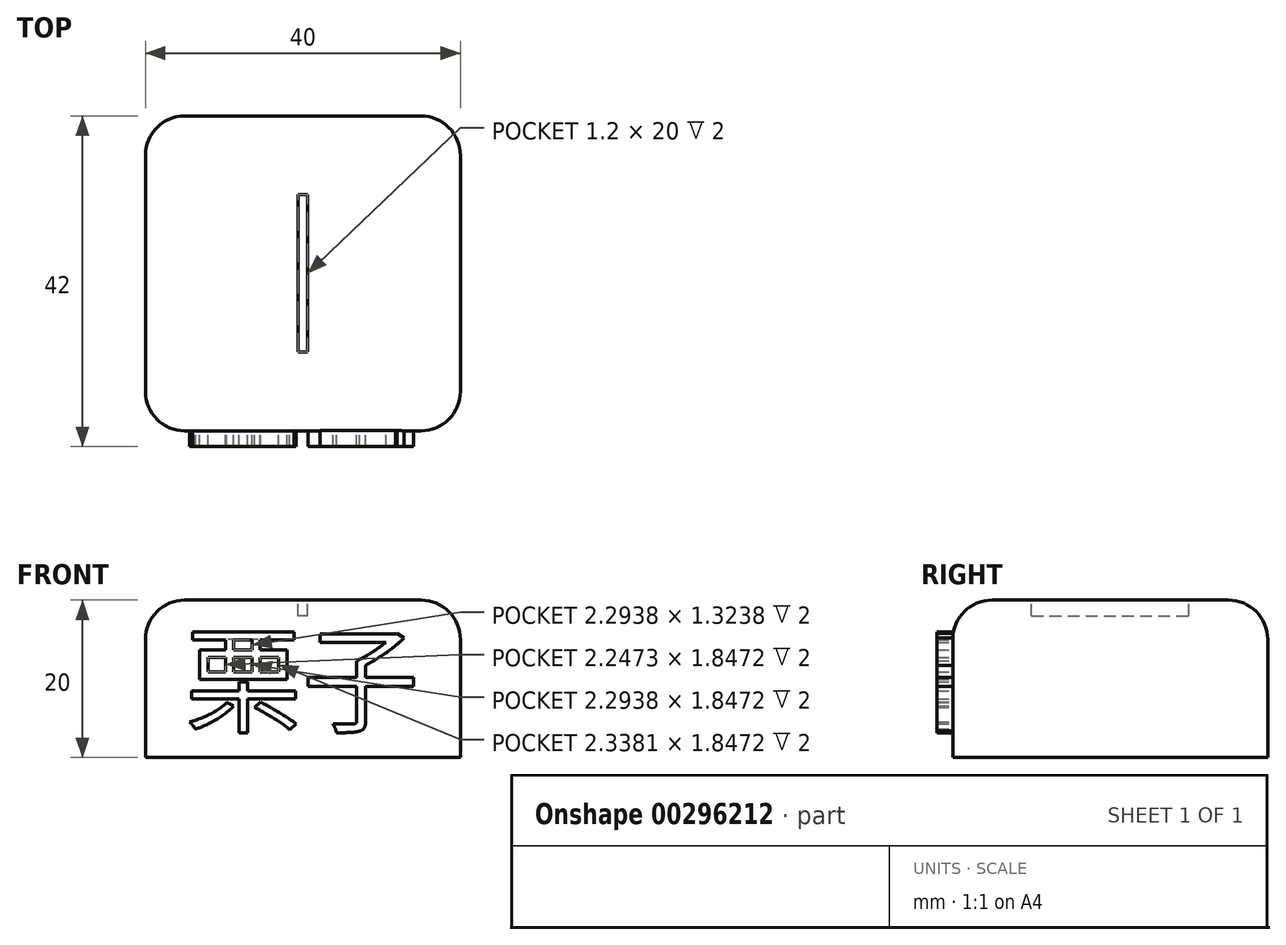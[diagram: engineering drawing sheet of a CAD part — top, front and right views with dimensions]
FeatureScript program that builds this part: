
annotation { "Feature Type Name" : "Feature", "Feature Type Description" : "" }
export const myFeature = defineFeature(function(context is Context, id is Id, definition is map)
    precondition{}
    {
        {
            var Q0;
            Q0=qCreatedBy(makeId("Top.planeOp"),FACE);
            var sketch = newSketch(context, id + "F0", { "sketchPlane" : qUnion([Q0])});
            skLineSegment(sketch, "E0.bottom", {"start": v(20, -20) * mm, "end": v(-20, -20) * mm});
            skLineSegment(sketch, "E0.top", {"start": v(20, 20) * mm, "end": v(-20, 20) * mm});
            skLineSegment(sketch, "E0.left", {"start": v(20, -20) * mm, "end": v(20, 20) * mm});
            skLineSegment(sketch, "E0.right", {"start": v(-20, -20) * mm, "end": v(-20, 20) * mm});
            skPoint(sketch, "E0.middle", {"position": v(0, 0) * mm});
            skLineSegment(sketch, "E1.bottom", {"start": v(0.6, -10) * mm, "end": v(-0.6, -10) * mm});
            skLineSegment(sketch, "E1.top", {"start": v(0.6, 10) * mm, "end": v(-0.6, 10) * mm});
            skLineSegment(sketch, "E1.left", {"start": v(0.6, -10) * mm, "end": v(0.6, 10) * mm});
            skLineSegment(sketch, "E1.right", {"start": v(-0.6, -10) * mm, "end": v(-0.6, 10) * mm});
            skSolve(sketch);
        }
        {
            var Q0;
            Q0=makeQuery(id+"F0.imprint","IMPRINT",FACE,{"disambiguationData":[TD([[makeQuery(id+"F0.imprint","IMPRINT",EDGE,{"derivedFrom":sQuery(id+"F0.wireOp",EDGE,"E0.bottom")}),-1.0]])]});
            var Q1;
            Q1=makeQuery(id+"F0.imprint","IMPRINT",FACE,{"disambiguationData":[TD([[makeQuery(id+"F0.imprint","IMPRINT",EDGE,{"derivedFrom":sQuery(id+"F0.wireOp",EDGE,"E1.bottom")}),-1.0]])]});
            extrude(context, id + "F1", {"entities" : qUnion([Q0, Q1]), "oppositeDirection" : true, "depth" : 20 * mm});
        }
        {
            var Q0;
            Q0=makeQuery(id+"F0.imprint","IMPRINT",FACE,{"disambiguationData":[TD([[makeQuery(id+"F0.imprint","IMPRINT",EDGE,{"derivedFrom":sQuery(id+"F0.wireOp",EDGE,"E1.bottom")}),-1.0]])]});
            extrude(context, id + "F2", {"entities" : qUnion([Q0]), "operationType" : NewBodyOperationType.REMOVE, "oppositeDirection" : true, "depth" : 2 * mm});
        }
        {
            var Q0;
            Q0=makeQuery(id+"F2.boolean.opBoolean","COPY",EDGE,{"derivedFrom":makeQuery(id+"F2.opExtrude","CAP_EDGE",EDGE,{"disambiguationData":[OSD([sQuery(id+"F0.wireOp",EDGE,"E1.left")])],"isStart":true})});
            var Q1;
            Q1=makeQuery(id+"F2.boolean.opBoolean","COPY",EDGE,{"derivedFrom":makeQuery(id+"F2.opExtrude","CAP_EDGE",EDGE,{"disambiguationData":[OSD([sQuery(id+"F0.wireOp",EDGE,"E1.right")])],"isStart":true})});
            var Q2;
            Q2=makeQuery(id+"F1.opExtrude","SWEPT_EDGE",EDGE,{"disambiguationData":[OSD([sQuery(id+"F0.wireOp",EDGE,"E0.bottom"),sQuery(id+"F0.wireOp",EDGE,"E0.left")])]});
            var Q3;
            Q3=makeQuery(id+"F1.opExtrude","SWEPT_EDGE",EDGE,{"disambiguationData":[OSD([sQuery(id+"F0.wireOp",EDGE,"E0.top"),sQuery(id+"F0.wireOp",EDGE,"E0.left")])]});
            var Q4;
            Q4=makeQuery(id+"F1.opExtrude","CAP_EDGE",EDGE,{"disambiguationData":[OSD([sQuery(id+"F0.wireOp",EDGE,"E0.left")])],"isStart":true});
            var Q5;
            Q5=makeQuery(id+"F1.opExtrude","SWEPT_EDGE",EDGE,{"disambiguationData":[OSD([sQuery(id+"F0.wireOp",EDGE,"E0.bottom"),sQuery(id+"F0.wireOp",EDGE,"E0.right")])]});
            var Q6;
            Q6=makeQuery(id+"F1.opExtrude","SWEPT_EDGE",EDGE,{"disambiguationData":[OSD([sQuery(id+"F0.wireOp",EDGE,"E0.top"),sQuery(id+"F0.wireOp",EDGE,"E0.right")])]});
            var Q7;
            Q7=makeQuery(id+"F1.opExtrude","CAP_EDGE",EDGE,{"disambiguationData":[OSD([sQuery(id+"F0.wireOp",EDGE,"E0.top")])],"isStart":true});
            var Q8;
            Q8=makeQuery(id+"F1.opExtrude","CAP_EDGE",EDGE,{"disambiguationData":[OSD([sQuery(id+"F0.wireOp",EDGE,"E0.right")])],"isStart":true});
            var Q9;
            Q9=makeQuery(id+"F1.opExtrude","CAP_EDGE",EDGE,{"disambiguationData":[OSD([sQuery(id+"F0.wireOp",EDGE,"E0.bottom")])],"isStart":true});
            fillet(context, id + "F3", {"entities" : qUnion([Q0, Q1, Q2, Q3, Q4, Q5, Q6, Q7, Q8, Q9]), "radius" : 5 * mm, "tangentPropagation" : true, "allowEdgeOverflow" : false});
        }
        {
            var Q0;
            Q0=makeQuery(id+"F1.opExtrude","SWEPT_FACE",FACE,{"disambiguationData":[OSD([sQuery(id+"F0.wireOp",EDGE,"E0.bottom")])]});
            var sketch = newSketch(context, id + "F4", { "sketchPlane" : qUnion([Q0])});
            skText(sketch, "E2", { "text": "栗子", "fontName": "NotoSansCJKtc-Regular.otf"});
            const initialGuessF4  = {"E2": [-0.015, -0.01572, 1, 0, 0.01072]};
            skSetInitialGuess(sketch, initialGuessF4);
            skSolve(sketch);
        }
        {
            var Q0;
            Q0=makeQuery(id+"F4.imprint","IMPRINT",FACE,{"disambiguationData":[TD([[makeQuery(id+"F4.imprint","IMPRINT",EDGE,{"derivedFrom":sQuery(id+"F4.wireOp",EDGE,"E2.sketch_text.stroke-0")}),1.0]])]});
            var Q1;
            {var subQ1=sQuery(id+"F4.wireOp",EDGE,"E2.sketch_text.stroke-51");Q1=makeQuery(id+"F4.imprint","IMPRINT",FACE,{"disambiguationData":[TD([[makeQuery(id+"F4.imprint","IMPRINT",EDGE,{"derivedFrom":subQ1}),1.0]])]});}
            var Q2;
            {var subQ0=sQuery(id+"F4.wireOp",EDGE,"E2.sketch_text.stroke-24");Q2=makeQuery(id+"F4.imprint","IMPRINT",FACE,{"disambiguationData":[TD([[makeQuery(id+"F4.imprint","IMPRINT",EDGE,{"derivedFrom":subQ0}),1.0]])]});}
            var Q3;
            Q3=makeQuery(id+"F4.imprint","IMPRINT",FACE,{"disambiguationData":[TD([[makeQuery(id+"F4.imprint","IMPRINT",EDGE,{"derivedFrom":sQuery(id+"F4.wireOp",EDGE,"E2.sketch_text.stroke-32")}),1.0]])]});
            var Q4;
            Q4=makeQuery(id+"F4.imprint","IMPRINT",FACE,{"disambiguationData":[TD([[makeQuery(id+"F4.imprint","IMPRINT",EDGE,{"derivedFrom":sQuery(id+"F4.wireOp",EDGE,"E2.sketch_text.stroke-28")}),1.0]])]});
            var Q5;
            Q5=makeQuery(id+"F4.imprint","IMPRINT",FACE,{"disambiguationData":[TD([[makeQuery(id+"F4.imprint","IMPRINT",EDGE,{"derivedFrom":sQuery(id+"F4.wireOp",EDGE,"E2.sketch_text.stroke-44")}),1.0]])]});
            extrude(context, id + "F5", {"entities" : qUnion([Q0, Q1, Q2, Q3, Q4, Q5]), "operationType" : NewBodyOperationType.ADD, "depth" : 2 * mm});
        }
        {
            var Q0;
            Q0=makeQuery(id+"F5.opExtrude","CAP_FACE",FACE,{"disambiguationData":[OSD([sQuery(id+"F0.wireOp",EDGE,"E0.bottom"),sQuery(id+"F4.wireOp",EDGE,"E2.sketch_text.stroke-50"),sQuery(id+"F4.wireOp",EDGE,"E2.sketch_text.stroke-51"),sQuery(id+"F4.wireOp",EDGE,"E2.sketch_text.stroke-52"),sQuery(id+"F4.wireOp",EDGE,"E2.sketch_text.stroke-53"),sQuery(id+"F4.wireOp",EDGE,"E2.sketch_text.stroke-54")])],"isStart":false});
            extrude(context, id + "F6", {"entities" : qUnion([Q0]), "operationType" : NewBodyOperationType.ADD, "oppositeDirection" : true, "depth" : 3 * mm});
        }
        {
            var Q0;
            Q0=makeQuery(id+"F4.imprint","IMPRINT",FACE,{"disambiguationData":[TD([[makeQuery(id+"F4.imprint","IMPRINT",EDGE,{"derivedFrom":sQuery(id+"F4.wireOp",EDGE,"E2.sketch_text.stroke-48")}),1.0]])]});
            extrude(context, id + "F7", {"entities" : qUnion([Q0]), "operationType" : NewBodyOperationType.ADD, "depth" : 2 * mm});
        }
    });
